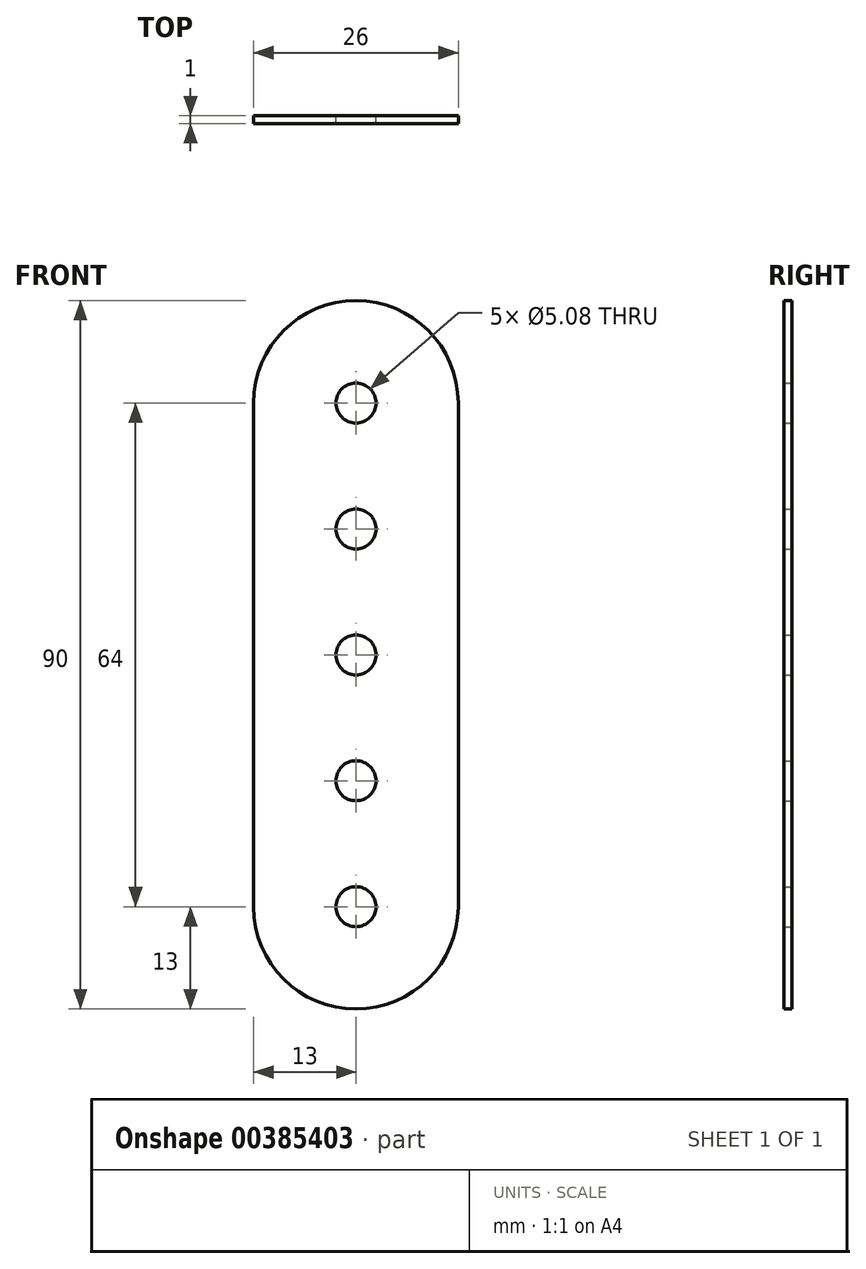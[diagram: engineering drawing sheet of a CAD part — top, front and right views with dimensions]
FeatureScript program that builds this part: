
annotation { "Feature Type Name" : "Feature", "Feature Type Description" : "" }
export const myFeature = defineFeature(function(context is Context, id is Id, definition is map)
    precondition{}
    {
        {
            var Q0;
            Q0=qCreatedBy(makeId("Front.planeOp"),FACE);
            var sketch = newSketch(context, id + "F0", { "sketchPlane" : qUnion([Q0])});
            skLineSegment(sketch, "E0", {"start": v(-13, 48) * mm, "end": v(-13, -16) * mm});
            skLineSegment(sketch, "E1", {"start": v(13, -16) * mm, "end": v(13, 48) * mm});
            skCircle(sketch, "E2", {"center": v(0, 48) * mm, "radius": 2.54 * mm});
            skCircle(sketch, "E3", {"center": v(0, -16) * mm, "radius": 2.54 * mm});
            skPoint(sketch, "E4", {"position": v(0, 32) * mm});
            skCircle(sketch, "E5", {"center": v(0, 32) * mm, "radius": 2.54 * mm});
            skCircle(sketch, "E6", {"center": v(0, 48) * mm, "radius": 13 * mm});
            skCircle(sketch, "E7", {"center": v(0, -16) * mm, "radius": 13 * mm});
            skCircle(sketch, "E8.0.1.0", {"center": v(0, 16) * mm, "radius": 2.54 * mm});
            skCircle(sketch, "E8.0.2.0", {"center": v(0, 0) * mm, "radius": 2.54 * mm});
            skSolve(sketch);
        }
        {
            var Q0;
            Q0=qSketchRegion(id+"F0",true);
            extrude(context, id + "F1", {"entities" : qUnion([Q0]), "depth" : 1 * mm});
        }
    });
